# Revit family: LA2C-End Round
name_source: partatom
category: Lighting Fixtures
revit_build: Autodesk Revit 2014 (Build: 20130709_2115(x64)
units: mm (PartAtom-declared; Revit-internal decimal feet)

## types (1)
- End Round
    Color Filter = 16777215
    Comments = This model is for use in spatial massing and rendering. Please contact LightArt for pick-point placement and installation details.
    Description = LED System
    Diffuser = White Opal Acrylic
    Dimming Compatibility = 0-10v
    Dimming Lamp Color Temperature Shift = <None>
    Driver = 24v
    HARDWARE = Removable powder coated lid


3/64” stainless steel cables to canopy 

Adjustable 24”-96” suspension
    Hardware = Stainless Steel Cables
    Height = 0' - 8"
    Height From Face = 4' - 0"
    Input = 120v-277v
    LIGHTING = Solid State LED System
120v-277v input; 24v driver;
0-10v dimming compatible
3000k 81 CRI light source
S - 14w, 1050mA, 1045 lumens
    Left = No
    Light Source Symbol Size = 0' - 6"
    Manufacturer = LightArt
    Model = LA2C
    STANDARDS = 6-8 week lead time, Damp rated, UL Compliant / CSA Approved
    Shade = 3form Varia Ecoresin
    Type Comments = Stainless steel canopy mounts to
standard junction box (provided by others)
    Weight = 8 lbs
    Width = 0' - 6"

## geometry (parser evidence)
native form markers: Blend x2, Sweep x5
no freeform markers — native parametric forms only
